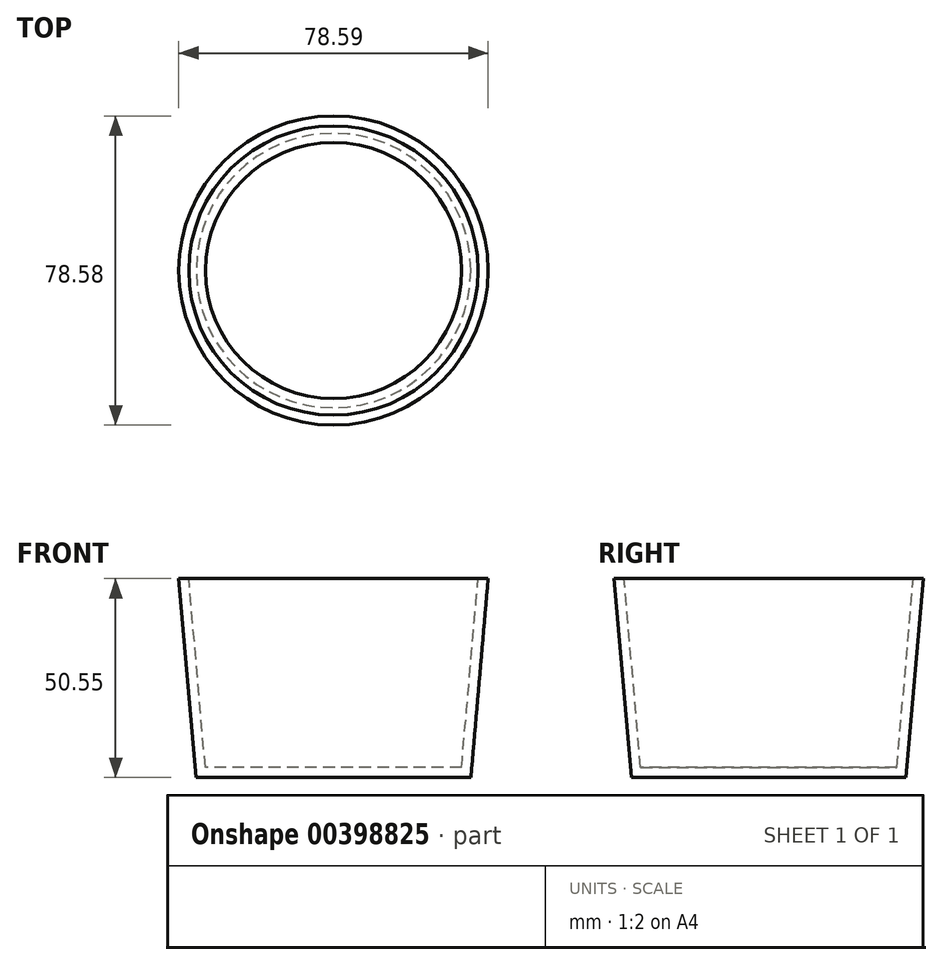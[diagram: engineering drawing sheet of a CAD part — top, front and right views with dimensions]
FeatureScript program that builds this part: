
annotation { "Feature Type Name" : "Feature", "Feature Type Description" : "" }
export const myFeature = defineFeature(function(context is Context, id is Id, definition is map)
    precondition{}
    {
        {
            var Q0;
            Q0=qCreatedBy(makeId("Top.planeOp"),FACE);
            var sketch = newSketch(context, id + "F0", { "sketchPlane" : qUnion([Q0])});
            skCircle(sketch, "E0", {"center": v(-12.04, 0) * mm, "radius": 34.87 * mm});
            skLineSegment(sketch, "E1", {"start": v(-12.04, 0) * mm, "end": v(17.95, 17.79) * mm});
            skLineSegment(sketch, "E2", {"start": v(17.95, 17.79) * mm, "end": v(17.95, 17.79) * mm});
            skSolve(sketch);
        }
        {
            var Q0;
            Q0 = qSketchRegion(id + "F0", true);
            extrude(context, id + "F1", {"entities" : qUnion([Q0]), "depth" : 50.55 * mm, "hasDraft" : true, "draftAngle" : 5 * degree});
        }
        {
            var Q0;
            Q0=makeQuery(id+"F1.opExtrude","CAP_FACE",FACE,{"disambiguationData":[OSD([sQuery(id+"F0.wireOp",EDGE,"E0")])],"isStart":false});
            shell(context, id + "F2", {"entities" : qUnion([Q0]), "thickness" : 2.54 * mm});
        }
    });
